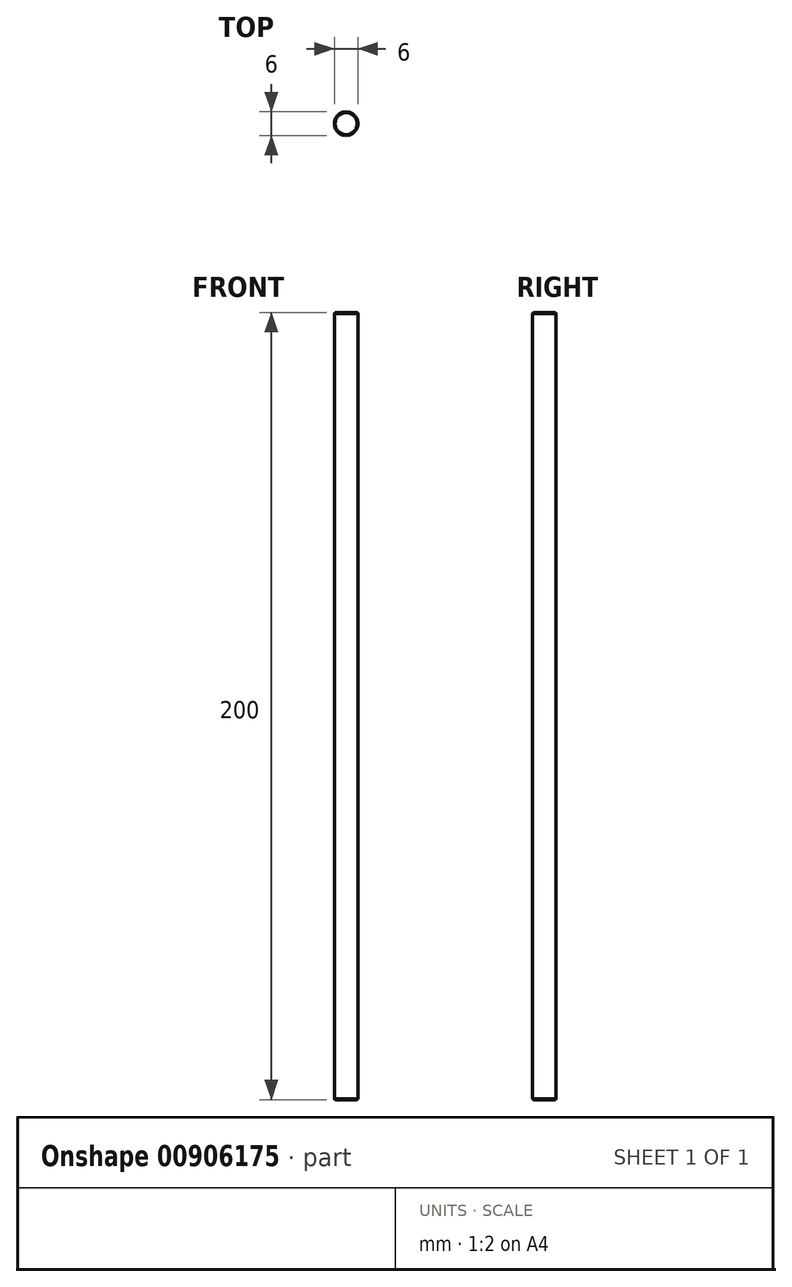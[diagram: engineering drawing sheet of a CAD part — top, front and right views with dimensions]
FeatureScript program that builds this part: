
annotation { "Feature Type Name" : "Feature", "Feature Type Description" : "" }
export const myFeature = defineFeature(function(context is Context, id is Id, definition is map)
    precondition{}
    {
        {
            var Q0;
            Q0=qCreatedBy(makeId("Top.planeOp"),FACE);
            var sketch = newSketch(context, id + "F0", { "sketchPlane" : qUnion([Q0])});
            skCircle(sketch, "E0", {"center": v(0, 0) * mm, "radius": 3 * mm});
            skSolve(sketch);
        }
        {
            var Q0;
            Q0 = qSketchRegion(id + "F0", true);
            extrude(context, id + "F1", {"entities" : qUnion([Q0]), "depth" : 200 * mm, "offsetDistance" : 25 * mm});
        }
        {
            var Q0;
            Q0=makeQuery(id+"F1.opExtrude","CAP_EDGE",EDGE,{"disambiguationData":[OSD([sQuery(id+"F0.wireOp",EDGE,"E0")])],"isStart":false});
            var Q1;
            Q1=makeQuery(id+"F1.opExtrude","CAP_EDGE",EDGE,{"disambiguationData":[OSD([sQuery(id+"F0.wireOp",EDGE,"E0")])],"isStart":true});
            chamfer(context, id + "F2", {"entities" : qUnion([Q0, Q1]), "width" : 0.2 * mm});
        }
    });
